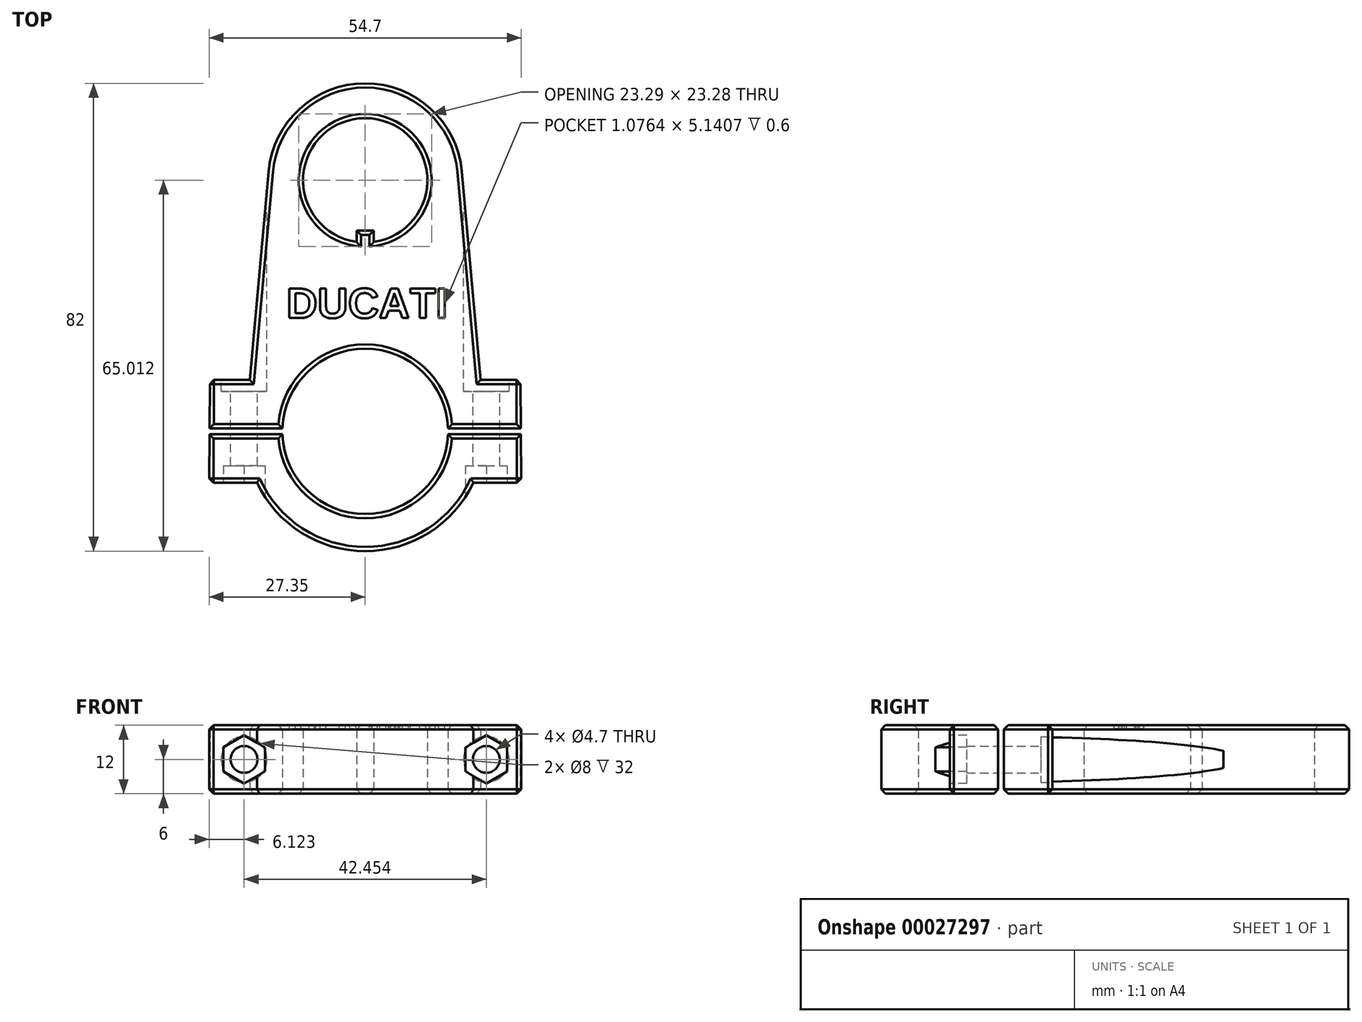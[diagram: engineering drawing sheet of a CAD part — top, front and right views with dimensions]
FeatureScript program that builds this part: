
annotation { "Feature Type Name" : "Feature", "Feature Type Description" : "" }
export const myFeature = defineFeature(function(context is Context, id is Id, definition is map)
    precondition{}
    {
        {
            var Q0;
            Q0=qCreatedBy(makeId("Top.planeOp"),FACE);
            var sketch = newSketch(context, id + "F0", { "sketchPlane" : qUnion([Q0])});
            skArc(sketch, "E0", {"start": v(1.5, 33.2) * mm, "mid": v(0, 54.9) * mm, "end": v(-1.5, 33.2) * mm});
            skCircle(sketch, "E1", {"center": v(0, 44) * mm, "radius": 17 * mm});
            skLineSegment(sketch, "E2.top", {"start": v(-1.5, 35.2) * mm, "end": v(1.5, 35.2) * mm});
            skLineSegment(sketch, "E2.left", {"start": v(-1.5, 33.2) * mm, "end": v(-1.5, 35.2) * mm});
            skLineSegment(sketch, "E2.right", {"start": v(1.5, 33.2) * mm, "end": v(1.5, 35.2) * mm});
            skArc(sketch, "E3", {"start": v(-14.5, -0.5) * mm, "mid": v(0, -14.5) * mm, "end": v(14.5, -0.5) * mm});
            skArc(sketch, "E4", {"start": v(-21, -0.5) * mm, "mid": v(0, -21) * mm, "end": v(21, -0.5) * mm});
            skLineSegment(sketch, "E5.bottom", {"start": v(-21, 0.5) * mm, "end": v(-14.5, 0.5) * mm});
            skLineSegment(sketch, "E5.top", {"start": v(-21, -0.5) * mm, "end": v(-14.5, -0.5) * mm});
            skArc(sketch, "E6.trimOffspring", {"start": v(14.5, 0.5) * mm, "mid": v(0, 14.5) * mm, "end": v(-14.5, 0.5) * mm});
            skLineSegment(sketch, "E7", {"start": v(-16.93, 45.53) * mm, "end": v(-20.23, 9) * mm});
            skLineSegment(sketch, "E8", {"start": v(16.93, 45.53) * mm, "end": v(20.23, 9) * mm});
            skLineSegment(sketch, "E9.bottom", {"start": v(-20.23, 9) * mm, "end": v(-27.23, 9) * mm});
            skLineSegment(sketch, "E9.right", {"start": v(-27.23, 9) * mm, "end": v(-27.29, 0.5) * mm});
            skLineSegment(sketch, "E10", {"start": v(-27.35, -9) * mm, "end": v(-18.97, -9) * mm});
            skLineSegment(sketch, "E11", {"start": v(-21, -0.5) * mm, "end": v(-27.3, -0.5) * mm});
            skLineSegment(sketch, "E12", {"start": v(-21, 0.5) * mm, "end": v(-27.29, 0.5) * mm});
            skLineSegment(sketch, "E13.trimOffspring", {"start": v(-27.3, -0.5) * mm, "end": v(-27.35, -9) * mm});
            skLineSegment(sketch, "E14.MirrorCS", {"start": v(20.23, 9) * mm, "end": v(27.23, 9) * mm});
            skLineSegment(sketch, "E15.MirrorCS", {"start": v(21, 0.5) * mm, "end": v(27.29, 0.5) * mm});
            skLineSegment(sketch, "E16.MirrorCS", {"start": v(21, -0.5) * mm, "end": v(27.3, -0.5) * mm});
            skLineSegment(sketch, "E17.MirrorCS", {"start": v(27.35, -9) * mm, "end": v(18.97, -9) * mm});
            skLineSegment(sketch, "E18.MirrorCS", {"start": v(27.3, -0.5) * mm, "end": v(27.35, -9) * mm});
            skLineSegment(sketch, "E19.MirrorCS", {"start": v(27.23, 9) * mm, "end": v(27.29, 0.5) * mm});
            skLineSegment(sketch, "E20.trimOffspring", {"start": v(14.5, 0.5) * mm, "end": v(21, 0.5) * mm});
            skLineSegment(sketch, "E21.trimOffspring", {"start": v(14.5, -0.5) * mm, "end": v(21, -0.5) * mm});
            skSolve(sketch);
        }
        {
            var Q0;
            Q0=qSketchRegion(id+"F0",true);
            extrude(context, id + "F1", {"entities" : qUnion([Q0]), "depth" : 12 * mm});
        }
        {
            var Q0;
            Q0=makeQuery(id+"F1.opExtrude","CAP_FACE",FACE,{"disambiguationData":[OSD([sQuery(id+"F0.wireOp",EDGE,"609e1772-262a-4104-8462-8853dac53054"),sQuery(id+"F0.wireOp",EDGE,"8b4357be-e4cc-448e-9bb4-f51b5584e2a0"),sQuery(id+"F0.wireOp",EDGE,"E0"),sQuery(id+"F0.wireOp",EDGE,"E1"),sQuery(id+"F0.wireOp",EDGE,"5a310b6e-eab9-4b47-9328-372e46da4570.top"),sQuery(id+"F0.wireOp",EDGE,"5a310b6e-eab9-4b47-9328-372e46da4570.left"),sQuery(id+"F0.wireOp",EDGE,"5a310b6e-eab9-4b47-9328-372e46da4570.right"),sQuery(id+"F0.wireOp",EDGE,"d20c0165-6708-49ba-9ae4-bde342b20082.left"),sQuery(id+"F0.wireOp",EDGE,"d20c0165-6708-49ba-9ae4-bde342b20082.right"),sQuery(id+"F0.wireOp",EDGE,"0f12ed5d-3162-4d45-9498-122dfb930fe9.trimOffspring"),sQuery(id+"F0.wireOp",EDGE,"85f25d08-1e02-4a9e-8e6b-932345104bb3"),sQuery(id+"F0.wireOp",EDGE,"2ffdacbe-6a5a-47ab-8ffc-9a737e2f0771")])],"isStart":false});
            var sketch = newSketch(context, id + "F2", { "sketchPlane" : qUnion([Q0])});
            skText(sketch, "E22", { "text": "DUCATI", "fontName": "Arimo-Bold.ttf"});
            const initialGuessF2  = {"E22": [-0.01378, 0.01987, 1, 0, 0.00538]};
            skSetInitialGuess(sketch, initialGuessF2);
            skSolve(sketch);
        }
        {
            var Q0;
            Q0=qSketchRegion(id+"F2",true);
            extrude(context, id + "F3", {"entities" : qUnion([Q0]), "operationType" : NewBodyOperationType.REMOVE, "oppositeDirection" : true, "depth" : .6 * mm});
        }
        {
            var Q0;
            Q0=makeQuery(id+"F1.opExtrude","SWEPT_FACE",FACE,{"disambiguationData":[OSD([sQuery(id+"F0.wireOp",EDGE,"E14.MirrorCS")])]});
            var sketch = newSketch(context, id + "F4", { "sketchPlane" : qUnion([Q0])});
            skCircle(sketch, "E23", {"center": v(-21.23, 6) * mm, "radius": 2.35 * mm});
            skCircle(sketch, "E24", {"center": v(21.23, 6) * mm, "radius": 2.35 * mm});
            skSolve(sketch);
        }
        {
            var Q0;
            Q0 = qSketchRegion(id + "F4", true);
            extrude(context, id + "F5", {"entities" : qUnion([Q0]), "operationType" : NewBodyOperationType.REMOVE, "oppositeDirection" : true, "depth" : 25 * mm});
        }
        {
            var Q0;
            Q0=makeQuery(id+"F1.opExtrude","SWEPT_FACE",FACE,{"disambiguationData":[OSD([sQuery(id+"F0.wireOp",EDGE,"E16.MirrorCS"),sQuery(id+"F0.wireOp",EDGE,"E21.trimOffspring")])]});
            var sketch = newSketch(context, id + "F6", { "sketchPlane" : qUnion([Q0])});
            skCircle(sketch, "E25", {"center": v(-21.23, 6) * mm, "radius": 2.35 * mm});
            skCircle(sketch, "E26.MirrorC", {"center": v(21.23, 6) * mm, "radius": 2.35 * mm});
            skSolve(sketch);
        }
        {
            var Q0;
            Q0 = qSketchRegion(id + "F6", true);
            extrude(context, id + "F7", {"entities" : qUnion([Q0]), "operationType" : NewBodyOperationType.REMOVE, "oppositeDirection" : true, "depth" : 25 * mm});
        }
        {
            var Q0;
            Q0=makeQuery(id+"F1.opExtrude","SWEPT_FACE",FACE,{"disambiguationData":[OSD([sQuery(id+"F0.wireOp",EDGE,"E14.MirrorCS")])]});
            cPlane(context, id + "F8", {"entities" : qUnion([Q0]), "cplaneType" : CPlaneType.OFFSET, "offset" : 30 * mm, "width" : 150 * mm, "height" : 150 * mm});
        }
        {
            var Q0;
            Q0=qCreatedBy(id+"F8.planeOp",FACE);
            var sketch = newSketch(context, id + "F9", { "sketchPlane" : qUnion([Q0])});
            skCircle(sketch, "E27", {"center": v(-21.23, 6) * mm, "radius": 4 * mm});
            skCircle(sketch, "E28", {"center": v(21.23, 6) * mm, "radius": 4 * mm});
            skSolve(sketch);
        }
        {
            var Q0;
            Q0=makeQuery(id+"F9.imprint","IMPRINT",FACE,{"disambiguationData":[TD([[makeQuery(id+"F9.imprint","IMPRINT",EDGE,{"derivedFrom":sQuery(id+"F9.wireOp",EDGE,"E27")}),1.0]])]});
            var Q1;
            Q1=makeQuery(id+"F9.imprint","IMPRINT",FACE,{"disambiguationData":[TD([[makeQuery(id+"F9.imprint","IMPRINT",EDGE,{"derivedFrom":sQuery(id+"F9.wireOp",EDGE,"E28")}),1.0]])]});
            extrude(context, id + "F10", {"entities" : qUnion([Q0, Q1]), "operationType" : NewBodyOperationType.REMOVE, "oppositeDirection" : true, "depth" : 32 * mm});
        }
        {
            var Q0;
            Q0=makeQuery(id+"F1.opExtrude","SWEPT_FACE",FACE,{"disambiguationData":[OSD([sQuery(id+"F0.wireOp",EDGE,"E17.MirrorCS")])]});
            cPlane(context, id + "F11", {"entities" : qUnion([Q0]), "cplaneType" : CPlaneType.OFFSET, "offset" : 10 * mm, "width" : 150 * mm, "height" : 150 * mm});
        }
        {
            var Q0;
            Q0=qCreatedBy(id+"F11.planeOp",FACE);
            var sketch = newSketch(context, id + "F12", { "sketchPlane" : qUnion([Q0])});
            skCircle(sketch, "E29.cCircle", {"center": v(21.23, 6) * mm, "radius": 3.65 * mm, "construction": true});
            skLineSegment(sketch, "E29.0", {"start": v(24.88, 8.1) * mm, "end": v(24.88, 3.9) * mm});
            skLineSegment(sketch, "E29.1", {"start": v(24.88, 3.9) * mm, "end": v(21.23, 1.79) * mm});
            skLineSegment(sketch, "E29.2", {"start": v(21.23, 1.79) * mm, "end": v(17.58, 3.9) * mm});
            skLineSegment(sketch, "E29.3", {"start": v(17.58, 3.9) * mm, "end": v(17.58, 8.1) * mm});
            skLineSegment(sketch, "E29.4", {"start": v(17.58, 8.1) * mm, "end": v(21.23, 10.21) * mm});
            skLineSegment(sketch, "E29.5", {"start": v(21.23, 10.21) * mm, "end": v(24.88, 8.1) * mm});
            skPoint(sketch, "E29.0.midPoint", {"position": v(24.88, 6) * mm});
            skLineSegment(sketch, "E30.MirrorCS", {"start": v(-24.88, 8.1) * mm, "end": v(-24.88, 3.9) * mm});
            skLineSegment(sketch, "E31.MirrorCS", {"start": v(-21.23, 1.79) * mm, "end": v(-17.58, 3.9) * mm});
            skLineSegment(sketch, "E32.MirrorCS", {"start": v(-17.58, 3.9) * mm, "end": v(-17.58, 8.1) * mm});
            skLineSegment(sketch, "E33.MirrorCS", {"start": v(-17.58, 8.1) * mm, "end": v(-21.23, 10.21) * mm});
            skLineSegment(sketch, "E34.MirrorCS", {"start": v(-24.88, 3.9) * mm, "end": v(-21.23, 1.79) * mm});
            skLineSegment(sketch, "E35.MirrorCS", {"start": v(-21.23, 10.21) * mm, "end": v(-24.88, 8.1) * mm});
            skPoint(sketch, "E36.MirrorP", {"position": v(-24.88, 6) * mm});
            skCircle(sketch, "E37.MirrorC", {"center": v(-21.23, 6) * mm, "radius": 3.65 * mm});
            skSolve(sketch);
        }
        {
            var Q0;
            Q0 = qSketchRegion(id + "F12", true);
            extrude(context, id + "F13", {"entities" : qUnion([Q0]), "operationType" : NewBodyOperationType.REMOVE, "oppositeDirection" : true, "depth" : 13 * mm});
        }
        {
            var Q0;
            Q0=makeQuery(id+"F1.opExtrude","CAP_EDGE",EDGE,{"disambiguationData":[OSD([sQuery(id+"F0.wireOp",EDGE,"E0")])],"isStart":false});
            var Q1;
            Q1=makeQuery(id+"F1.opExtrude","CAP_EDGE",EDGE,{"disambiguationData":[OSD([sQuery(id+"F0.wireOp",EDGE,"E2.left")])],"isStart":false});
            var Q2;
            Q2=makeQuery(id+"F1.opExtrude","CAP_EDGE",EDGE,{"disambiguationData":[OSD([sQuery(id+"F0.wireOp",EDGE,"E2.top")])],"isStart":false});
            var Q3;
            Q3=makeQuery(id+"F1.opExtrude","CAP_EDGE",EDGE,{"disambiguationData":[OSD([sQuery(id+"F0.wireOp",EDGE,"E2.right")])],"isStart":false});
            var Q4;
            Q4=makeQuery(id+"F1.opExtrude","CAP_EDGE",EDGE,{"disambiguationData":[OSD([sQuery(id+"F0.wireOp",EDGE,"E0")])],"isStart":true});
            var Q5;
            Q5=makeQuery(id+"F1.opExtrude","CAP_EDGE",EDGE,{"disambiguationData":[OSD([sQuery(id+"F0.wireOp",EDGE,"E2.right")])],"isStart":true});
            var Q6;
            Q6=makeQuery(id+"F1.opExtrude","CAP_EDGE",EDGE,{"disambiguationData":[OSD([sQuery(id+"F0.wireOp",EDGE,"E2.top")])],"isStart":true});
            var Q7;
            Q7=makeQuery(id+"F1.opExtrude","CAP_EDGE",EDGE,{"disambiguationData":[OSD([sQuery(id+"F0.wireOp",EDGE,"E2.left")])],"isStart":true});
            var Q8;
            Q8=makeQuery(id+"F1.opExtrude","CAP_EDGE",EDGE,{"disambiguationData":[OSD([sQuery(id+"F0.wireOp",EDGE,"E1")])],"isStart":true});
            var Q9;
            Q9=makeQuery(id+"F1.opExtrude","CAP_EDGE",EDGE,{"disambiguationData":[OSD([sQuery(id+"F0.wireOp",EDGE,"E14.MirrorCS")])],"isStart":true});
            var Q10;
            Q10=makeQuery(id+"F1.opExtrude","CAP_EDGE",EDGE,{"disambiguationData":[OSD([sQuery(id+"F0.wireOp",EDGE,"E19.MirrorCS")])],"isStart":true});
            var Q11;
            Q11=makeQuery(id+"F1.opExtrude","CAP_EDGE",EDGE,{"disambiguationData":[OSD([sQuery(id+"F0.wireOp",EDGE,"E15.MirrorCS"),sQuery(id+"F0.wireOp",EDGE,"E20.trimOffspring")])],"isStart":true});
            var Q12;
            Q12=makeQuery(id+"F1.opExtrude","CAP_EDGE",EDGE,{"disambiguationData":[OSD([sQuery(id+"F0.wireOp",EDGE,"E6.trimOffspring")])],"isStart":true});
            var Q13;
            Q13=makeQuery(id+"F1.opExtrude","CAP_EDGE",EDGE,{"disambiguationData":[OSD([sQuery(id+"F0.wireOp",EDGE,"E5.bottom"),sQuery(id+"F0.wireOp",EDGE,"E12")])],"isStart":true});
            var Q14;
            Q14=makeQuery(id+"F1.opExtrude","CAP_EDGE",EDGE,{"disambiguationData":[OSD([sQuery(id+"F0.wireOp",EDGE,"E9.right")])],"isStart":true});
            var Q15;
            Q15=makeQuery(id+"F1.opExtrude","CAP_EDGE",EDGE,{"disambiguationData":[OSD([sQuery(id+"F0.wireOp",EDGE,"E9.bottom")])],"isStart":true});
            var Q16;
            Q16=makeQuery(id+"F1.opExtrude","CAP_EDGE",EDGE,{"disambiguationData":[OSD([sQuery(id+"F0.wireOp",EDGE,"E9.right")])],"isStart":false});
            var Q17;
            Q17=makeQuery(id+"F1.opExtrude","CAP_EDGE",EDGE,{"disambiguationData":[OSD([sQuery(id+"F0.wireOp",EDGE,"E9.bottom")])],"isStart":false});
            var Q18;
            Q18=makeQuery(id+"F1.opExtrude","CAP_EDGE",EDGE,{"disambiguationData":[OSD([sQuery(id+"F0.wireOp",EDGE,"E7")])],"isStart":false});
            var Q19;
            Q19=makeQuery(id+"F1.opExtrude","CAP_EDGE",EDGE,{"disambiguationData":[OSD([sQuery(id+"F0.wireOp",EDGE,"E8")])],"isStart":false});
            var Q20;
            Q20=makeQuery(id+"F1.opExtrude","CAP_EDGE",EDGE,{"disambiguationData":[OSD([sQuery(id+"F0.wireOp",EDGE,"E14.MirrorCS")])],"isStart":false});
            var Q21;
            Q21=makeQuery(id+"F1.opExtrude","CAP_EDGE",EDGE,{"disambiguationData":[OSD([sQuery(id+"F0.wireOp",EDGE,"E19.MirrorCS")])],"isStart":false});
            var Q22;
            Q22=makeQuery(id+"F1.opExtrude","CAP_EDGE",EDGE,{"disambiguationData":[OSD([sQuery(id+"F0.wireOp",EDGE,"E15.MirrorCS"),sQuery(id+"F0.wireOp",EDGE,"E20.trimOffspring")])],"isStart":false});
            var Q23;
            Q23=makeQuery(id+"F1.opExtrude","CAP_EDGE",EDGE,{"disambiguationData":[OSD([sQuery(id+"F0.wireOp",EDGE,"E6.trimOffspring")])],"isStart":false});
            var Q24;
            Q24=makeQuery(id+"F1.opExtrude","CAP_EDGE",EDGE,{"disambiguationData":[OSD([sQuery(id+"F0.wireOp",EDGE,"E5.bottom"),sQuery(id+"F0.wireOp",EDGE,"E12")])],"isStart":false});
            var Q25;
            Q25=makeQuery(id+"F1.opExtrude","CAP_EDGE",EDGE,{"disambiguationData":[OSD([sQuery(id+"F0.wireOp",EDGE,"E3")])],"isStart":false});
            var Q26;
            Q26=makeQuery(id+"F1.opExtrude","CAP_EDGE",EDGE,{"disambiguationData":[OSD([sQuery(id+"F0.wireOp",EDGE,"E16.MirrorCS"),sQuery(id+"F0.wireOp",EDGE,"E21.trimOffspring")])],"isStart":false});
            var Q27;
            Q27=makeQuery(id+"F1.opExtrude","CAP_EDGE",EDGE,{"disambiguationData":[OSD([sQuery(id+"F0.wireOp",EDGE,"E18.MirrorCS")])],"isStart":false});
            var Q28;
            Q28=makeQuery(id+"F1.opExtrude","CAP_EDGE",EDGE,{"disambiguationData":[OSD([sQuery(id+"F0.wireOp",EDGE,"E17.MirrorCS")])],"isStart":false});
            var Q29;
            Q29=makeQuery(id+"F1.opExtrude","CAP_EDGE",EDGE,{"disambiguationData":[OSD([sQuery(id+"F0.wireOp",EDGE,"E4")])],"isStart":false});
            var Q30;
            Q30=makeQuery(id+"F1.opExtrude","CAP_EDGE",EDGE,{"disambiguationData":[OSD([sQuery(id+"F0.wireOp",EDGE,"E10")])],"isStart":false});
            var Q31;
            Q31=makeQuery(id+"F1.opExtrude","CAP_EDGE",EDGE,{"disambiguationData":[OSD([sQuery(id+"F0.wireOp",EDGE,"E4")])],"isStart":true});
            var Q32;
            Q32=makeQuery(id+"F1.opExtrude","CAP_EDGE",EDGE,{"disambiguationData":[OSD([sQuery(id+"F0.wireOp",EDGE,"E10")])],"isStart":true});
            var Q33;
            Q33=makeQuery(id+"F1.opExtrude","CAP_EDGE",EDGE,{"disambiguationData":[OSD([sQuery(id+"F0.wireOp",EDGE,"E13.trimOffspring")])],"isStart":true});
            var Q34;
            Q34=makeQuery(id+"F1.opExtrude","CAP_EDGE",EDGE,{"disambiguationData":[OSD([sQuery(id+"F0.wireOp",EDGE,"E17.MirrorCS")])],"isStart":true});
            var Q35;
            Q35=makeQuery(id+"F1.opExtrude","CAP_EDGE",EDGE,{"disambiguationData":[OSD([sQuery(id+"F0.wireOp",EDGE,"E18.MirrorCS")])],"isStart":true});
            var Q36;
            Q36=makeQuery(id+"F1.opExtrude","CAP_EDGE",EDGE,{"disambiguationData":[OSD([sQuery(id+"F0.wireOp",EDGE,"E16.MirrorCS"),sQuery(id+"F0.wireOp",EDGE,"E21.trimOffspring")])],"isStart":true});
            var Q37;
            Q37=makeQuery(id+"F1.opExtrude","CAP_EDGE",EDGE,{"disambiguationData":[OSD([sQuery(id+"F0.wireOp",EDGE,"E3")])],"isStart":true});
            var Q38;
            Q38=makeQuery(id+"F1.opExtrude","CAP_EDGE",EDGE,{"disambiguationData":[OSD([sQuery(id+"F0.wireOp",EDGE,"E5.top"),sQuery(id+"F0.wireOp",EDGE,"E11")])],"isStart":true});
            var Q39;
            Q39=makeQuery(id+"F1.opExtrude","CAP_EDGE",EDGE,{"disambiguationData":[OSD([sQuery(id+"F0.wireOp",EDGE,"E13.trimOffspring")])],"isStart":false});
            var Q40;
            Q40=makeQuery(id+"F1.opExtrude","CAP_EDGE",EDGE,{"disambiguationData":[OSD([sQuery(id+"F0.wireOp",EDGE,"E5.top"),sQuery(id+"F0.wireOp",EDGE,"E11")])],"isStart":false});
            var Q41;
            Q41=makeQuery(id+"F1.opExtrude","SWEPT_EDGE",EDGE,{"disambiguationData":[OSD([sQuery(id+"F0.wireOp",EDGE,"E9.bottom"),sQuery(id+"F0.wireOp",EDGE,"E9.right")])]});
            var Q42;
            Q42=makeQuery(id+"F1.opExtrude","SWEPT_EDGE",EDGE,{"disambiguationData":[OSD([sQuery(id+"F0.wireOp",EDGE,"E14.MirrorCS"),sQuery(id+"F0.wireOp",EDGE,"E19.MirrorCS")])]});
            var Q43;
            Q43=makeQuery(id+"F1.opExtrude","SWEPT_EDGE",EDGE,{"disambiguationData":[OSD([sQuery(id+"F0.wireOp",EDGE,"E10"),sQuery(id+"F0.wireOp",EDGE,"E13.trimOffspring")])]});
            var Q44;
            Q44=makeQuery(id+"F1.opExtrude","SWEPT_EDGE",EDGE,{"disambiguationData":[OSD([sQuery(id+"F0.wireOp",EDGE,"E17.MirrorCS"),sQuery(id+"F0.wireOp",EDGE,"E18.MirrorCS")])]});
            chamfer(context, id + "F14", {"entities" : qUnion([Q0, Q1, Q2, Q3, Q4, Q5, Q6, Q7, Q8, Q9, Q10, Q11, Q12, Q13, Q14, Q15, Q16, Q17, Q18, Q19, Q20, Q21, Q22, Q23, Q24, Q25, Q26, Q27, Q28, Q29, Q30, Q31, Q32, Q33, Q34, Q35, Q36, Q37, Q38, Q39, Q40, Q41, Q42, Q43, Q44]), "width" : .75 * mm, "tangentPropagation" : true});
        }
    });
